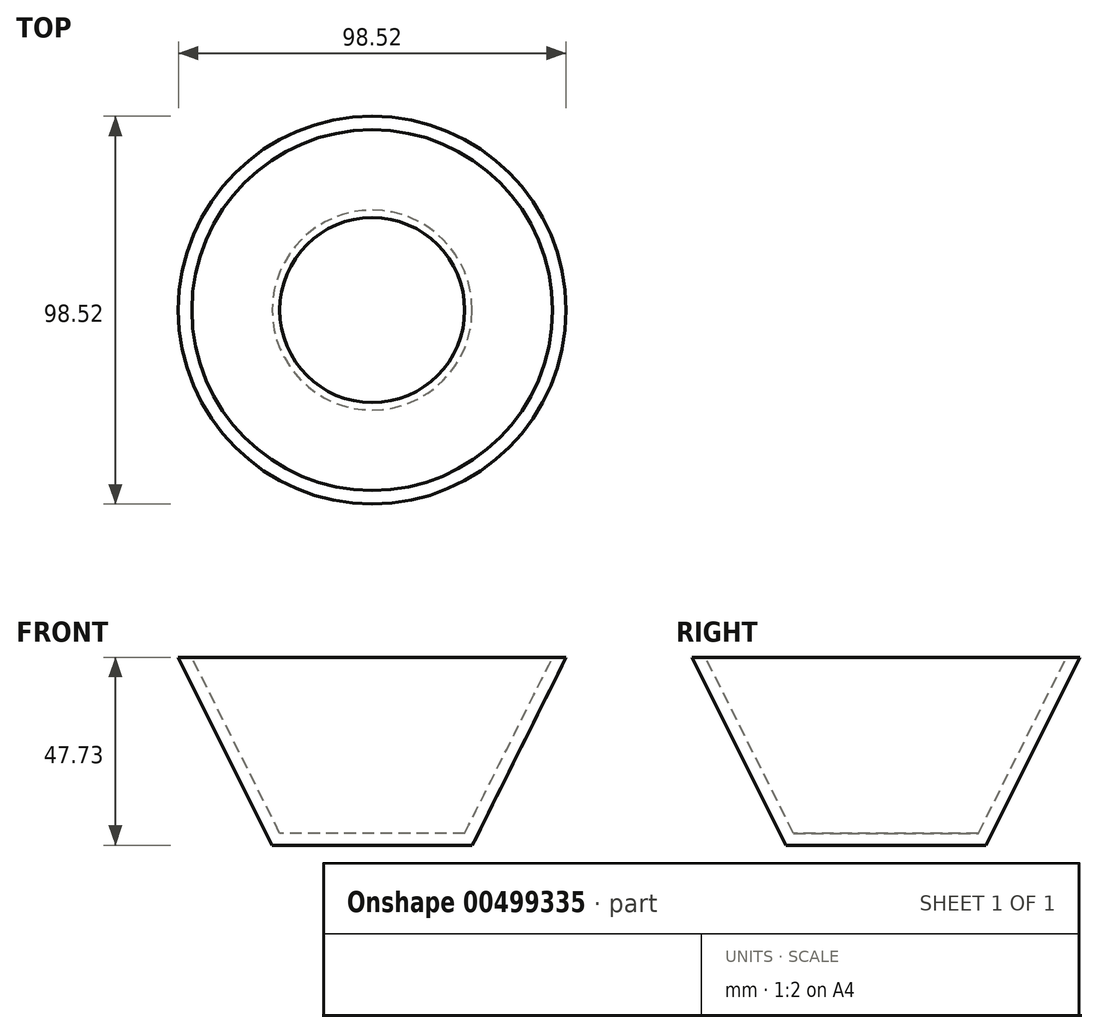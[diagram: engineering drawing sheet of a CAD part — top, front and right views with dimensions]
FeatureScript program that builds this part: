
annotation { "Feature Type Name" : "Feature", "Feature Type Description" : "" }
export const myFeature = defineFeature(function(context is Context, id is Id, definition is map)
    precondition{}
    {
        {
            var Q0;
            Q0=qCreatedBy(makeId("Front.planeOp"),FACE);
            var sketch = newSketch(context, id + "F0", { "sketchPlane" : qUnion([Q0])});
            skLineSegment(sketch, "E0", {"start": v(0, 0) * mm, "end": v(0, 47.73) * mm, "construction": true});
            skLineSegment(sketch, "E1", {"start": v(0, 0) * mm, "end": v(25.4, 0) * mm});
            skLineSegment(sketch, "E2", {"start": v(25.4, 0) * mm, "end": v(49.26, 47.73) * mm});
            skLineSegment(sketch, "E3.1", {"start": v(23.5, 3.07) * mm, "end": v(45.83, 47.73) * mm});
            skLineSegment(sketch, "E3.2", {"start": v(0, 3.07) * mm, "end": v(23.5, 3.07) * mm});
            skLineSegment(sketch, "E4", {"start": v(0, 3.07) * mm, "end": v(0, 0) * mm});
            skLineSegment(sketch, "E5", {"start": v(45.83, 47.73) * mm, "end": v(49.26, 47.73) * mm});
            skLineSegment(sketch, "E6", {"start": v(0, 47.73) * mm, "end": v(0, 3.07) * mm});
            skSolve(sketch);
        }
        {
            var Q0;
            Q0=makeQuery(id+"F0.imprint","IMPRINT",FACE,{"disambiguationData":[TD([[makeQuery(id+"F0.imprint","IMPRINT",EDGE,{"derivedFrom":sQuery(id+"F0.wireOp",EDGE,"E1")}),1.0]])]});
            var Q1;
            Q1=sQuery(id+"F0.wireOp",EDGE,"E6");
            revolve(context, id + "F1", {"entities" : qUnion([Q0]), "axis" : qUnion([Q1]), "revolveType" : RevolveType.FULL});
        }
    });
